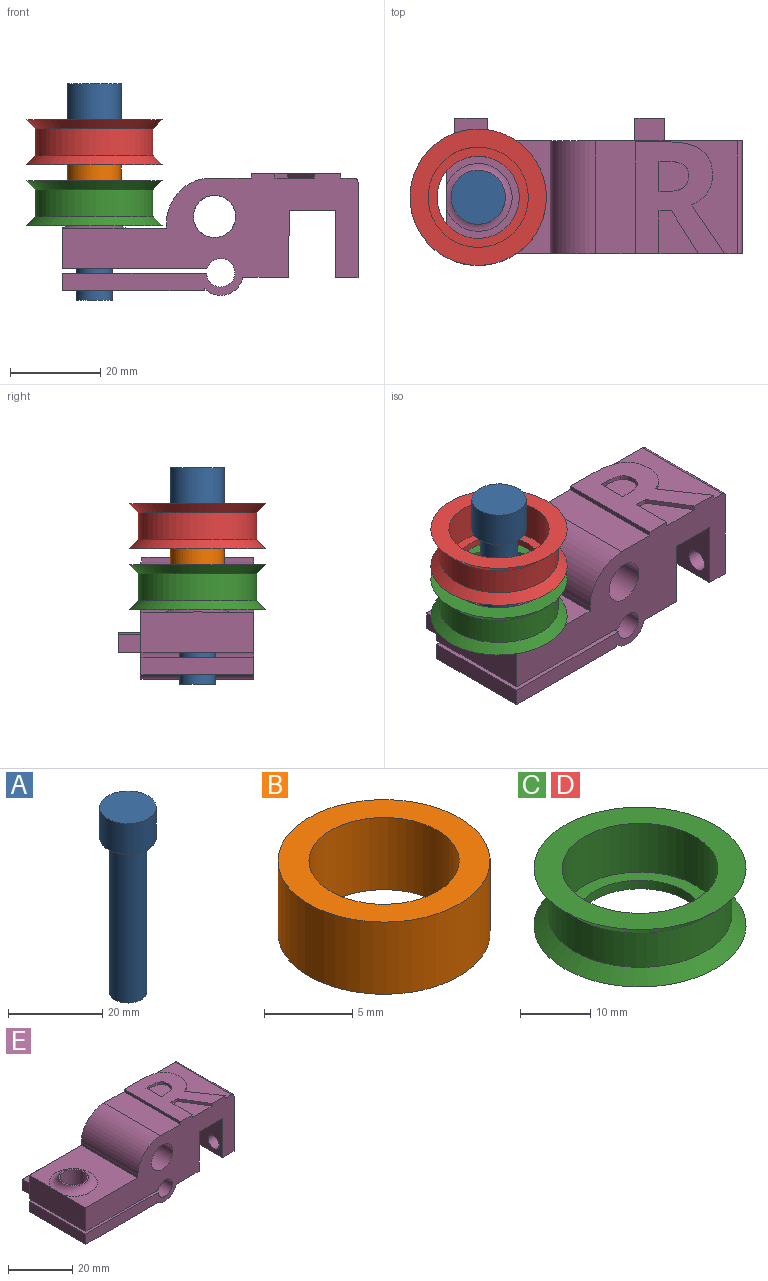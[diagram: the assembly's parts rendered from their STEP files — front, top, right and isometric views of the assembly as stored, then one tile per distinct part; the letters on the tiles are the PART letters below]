
ASSEMBLY  parts=5 mates=4
PART A: 5 faces, bbox 12x12x48 mm
  f0: cylinder r=4mm len=40mm, axis (0,0,-1), area 1005.3mm2, adj f1,f4
  f1: plane 8x8mm, normal (0,0,-1), area 50.3mm2, adj f0
  f2: cylinder r=6mm len=12mm, axis (0,0,-1), area 301.6mm2, adj f3,f4
  f3: plane 12x12mm, normal (0,0,1), area 113.1mm2, adj f2
  f4: plane 12x12mm, normal (0,0,-1), area 62.8mm2, adj f0,f2
PART B: 4 faces, bbox 12x12x5 mm
  f0: cylinder r=4.25mm len=8.5mm, axis (0,0,-1), area 133.5mm2, adj f2,f3
  f1: cylinder r=6mm len=12mm, axis (0,0,-1), area 188.5mm2, adj f2,f3
  f2: plane 12x12mm, normal (0,0,1), area 56.4mm2, adj f0,f1
  f3: plane 12x12mm, normal (0,0,-1), area 56.4mm2, adj f0,f1
PART C: 8 faces, bbox 30.2x30.2x10 mm
  f0: plane 30.2x30.2mm, normal (0,0,1), area 329.2mm2, adj f1,f7
  f1: cylinder r=11.1mm len=22.2mm, axis (0,0,-1), area 592.8mm2, adj f0,f2
  f2: plane 22.2x22.2mm, normal (0,0,1), area 126.9mm2, adj f1,f3
  f3: cylinder r=9.1mm len=18.2mm, axis (0,0,-1), area 85.8mm2, adj f2,f4
  f4: plane 30.2x30.2mm, normal (0,0,-1), area 456.2mm2, adj f3,f5
  f5: cone r=13.1mm half-angle=45deg, axis (0,0,-1), area 250.6mm2, adj f4,f6
  f6: cylinder r=13.1mm len=26.2mm, axis (0,0,-1), area 493.9mm2, adj f5,f7
  f7: cone r=15.1mm half-angle=45deg, axis (0,0,1), area 250.6mm2, adj f0,f6
PART D: same geometry as C
PART E: 57 faces, bbox 68.9x30x27 mm
  f0: plane 31.42x25mm, normal (0,0,1), area 392.1mm2, adj f15,f16,f26,f28,f41,f42,f43,f44
  f1: plane 9.51x8.71mm, normal (0,0,1), area 54.7mm2, adj f15,f38,f39,f40
  f2: plane 25x3.86mm, normal (-1,0,0), area 96.5mm2, adj f6,f15,f16,f20
  f3: cylinder r=4.17mm len=8.35mm, axis (0,0,1), area 101.3mm2, adj f6,f20
  f4: plane 25x10.1mm, normal (0,0,-1), area 252.6mm2, adj f14,f15,f16,f18
  f5: plane 25x0.6mm, normal (1,0,0), area 14.9mm2, adj f6,f15,f16,f18
  f6: plane 31.35x25mm, normal (0,0,-1), area 729mm2, adj f2,f3,f5,f15,f16
  f7: plane 25x9.08mm, normal (-1,0,0), area 226.1mm2, adj f8,f15,f16,f21,f25
  f8: plane 25x23mm, normal (0,0,1), area 400mm2, adj f7,f9,f15,f16,f25
  f9: plane 25x1.1mm, normal (-1,0,0), area 27.5mm2, adj f8,f15,f16,f26
  f10: plane 25x21.09mm, normal (1,0,0), area 493.5mm2, adj f11,f15,f16,f23,f24,f28
  f11: plane 25x5mm, normal (0,0,-1), area 125mm2, adj f10,f12,f15,f16
  f12: plane 25x15mm, normal (-1,0,0), area 341.3mm2, adj f11,f13,f15,f16,f23,f24
  f13: plane 25x10.2mm, normal (0,0,-1), area 255mm2, adj f12,f14,f15,f16
  f14: plane 25x14.91mm, normal (1,0,-0.01), area 372.8mm2, adj f4,f13,f15,f16
  f15: plane 65.42x27mm, normal (0,-1,0), area 1009.8mm2, adj f0,f1,f2,f4,f5,f6,f7,f8
  f16: plane 65.42x26mm, normal (0,1,0), area 938.8mm2, adj f0,f2,f4,f5,f6,f7,f8,f9
  f17: cylinder r=4.17mm len=11.04mm, axis (0,0,1), area 289.6mm2, adj f21,f22
  f18: cylinder r=5mm len=25mm, axis (0,-1,0), area 273.8mm2, adj f4,f5,f15,f16
  f19: cylinder r=3.15mm len=25mm, axis (0,-1,0), area 469.5mm2, adj f15,f16,f20,f21
  f20: plane 31.86x25mm, normal (0,0,1), area 741.8mm2, adj f2,f3,f15,f16,f19
  f21: plane 31.98x30mm, normal (0,0,-1), area 781.2mm2, adj f7,f15,f16,f17,f19,f30,f31,f32
  f22: plane 9.35x9.35mm, normal (0,0,1), area 13.9mm2, adj f17,f25
  f23: cylinder r=2.43mm len=5mm, axis (1,0,0), area 76.2mm2, adj f10,f12
  f24: cylinder r=2.2mm len=5mm, axis (1,0,0), area 69.1mm2, adj f10,f12
  f25: torus R=7.5mm, axis (0,0,-1), area 134.6mm2, adj f7,f8,f22
  f26: cylinder r=10mm len=25mm, axis (0,-1,0), area 392.7mm2, adj f0,f9,f15,f16
  f27: cylinder r=4.68mm len=25mm, axis (0,-1,0), area 735.2mm2, adj f15,f16
  f28: cylinder r=1mm len=25mm, axis (0,-1,0), area 39.3mm2, adj f0,f10,f15,f16
  f29: plane 7.3x5mm, normal (0,0,1), area 36.5mm2, adj f16,f30,f31,f32
  f30: plane 5x4.12mm, normal (-1,0,0), area 20.6mm2, adj f16,f21,f29,f32
  f31: plane 5x4.12mm, normal (1,0,0), area 20.6mm2, adj f16,f21,f29,f32
  f32: plane 7.3x4.12mm, normal (0,1,0), area 30.1mm2, adj f21,f29,f30,f31
  f33: plane 6.63x5mm, normal (0,0,1), area 33.2mm2, adj f16,f34,f36,f37
  f34: plane 5x4.5mm, normal (-1,0,0), area 22.5mm2, adj f16,f33,f35,f37
  f35: plane 6.63x5mm, normal (0,0,-1), area 33.2mm2, adj f16,f34,f36,f37
  f36: plane 5x4.5mm, normal (1,0,0), area 22.5mm2, adj f16,f33,f35,f37
  f37: plane 6.63x4.5mm, normal (0,1,0), area 29.9mm2, adj f33,f34,f35,f36
  f38: plane 9.51x1mm, normal (1,0,0), area 9.5mm2, adj f1,f15,f39,f55
  f39: plane 2.79x1mm, normal (0,-1,0), area 2.8mm2, adj f1,f38,f40,f55
  f40: plane 9.51x5.92mm, normal (-0.85,-0.53,0), area 11.2mm2, adj f1,f15,f39,f55
  f41: extruded ~10.8x7.29mm, area 13mm2, adj f0,f15,f42,f55
  f42: extruded ~3.41x2.67mm, area 4.4mm2, adj f0,f41,f43,f55
  f43: extruded ~3.89x1.2mm, area 4.1mm2, adj f0,f42,f44,f55
  f44: extruded ~5.59x2.42mm, area 6.3mm2, adj f0,f43,f45,f55
  f45: extruded ~7.48x1.84mm, area 7.8mm2, adj f0,f44,f46,f55
  f46: plane 7.22x1mm, normal (0,1,0), area 7.2mm2, adj f0,f45,f47,f55
  f47: plane 24.79x1mm, normal (-1,0,0), area 24.8mm2, adj f0,f15,f46,f55
  f48: plane 1.69x1mm, normal (0,1,0), area 1.7mm2, adj f49,f54,f55,f56
  f49: plane 6.7x1mm, normal (1,0,0), area 6.7mm2, adj f48,f50,f55,f56
  f50: plane 1.6x1mm, normal (0,-1,0), area 1.6mm2, adj f49,f51,f55,f56
  f51: extruded ~3.75x1mm, area 3.9mm2, adj f50,f52,f55,f56
  f52: extruded ~2.51x1.21mm, area 2.9mm2, adj f51,f53,f55,f56
  f53: extruded ~2.61x1.19mm, area 3mm2, adj f52,f54,f55,f56
  f54: extruded ~3.68x1mm, area 3.8mm2, adj f48,f53,f55,f56
  f55: plane 24.79x19.8mm, normal (0,0,1), area 300mm2, adj f15,f38,f39,f40,f41,f42,f43,f44
  f56: plane 6.7x6.56mm, normal (0,0,1), area 38.8mm2, adj f48,f49,f50,f51,f52,f53,f54
PLACE A t=(-103.78,-12.5,-5.1)mm
PLACE B rot(axis=(1,0,0),180deg) t=(-103.78,-12.5,24.9)mm
PLACE C t=(-103.78,-12.5,16.6)mm
PLACE D t=(-103.78,-12.5,30.1)mm
PLACE E at identity
MATE fastened A.f0 <-> D.f1  axis (0,0,-1) through (-103.78,-12.5,34.9)mm
MATE fastened B.f0 <-> C.f1  axis (0,0,1) through (-103.78,-12.5,19.9)mm
MATE fastened C.f1 <-> E.f3  axis (0,0,-1) through (-103.78,-12.5,11.4)mm
MATE fastened D.f1 <-> B.f0  axis (0,0,-1) through (-103.78,-12.5,24.9)mm
